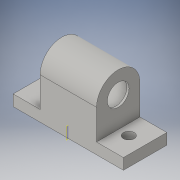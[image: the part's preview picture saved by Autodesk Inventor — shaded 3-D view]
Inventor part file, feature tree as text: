
AUTODESK INVENTOR PART (.ipt)
format: ipt  version: 2016 (Build 200138000, 138)  size: 147,968 bytes
history: native  units: in
note: dims shown in document units (in); Inventor stores cm internally (conversion verified against a paired STEP export)
features: extrude x4, sketch x4, projected_geometry x3, plane x1
ambient origin geometry x8: Origin, YZ Plane, XZ Plane, XY Plane, X Axis, Y Axis, Z Axis, Center Point
bodies: Solid1 (feature_tree)
feature tree (12):
  extrude  "Extrusion1"  Depth=0.7874in
  plane  "Work Plane1"
  extrude  "Extrusion2"  Depth=0.1969in
  extrude  "Extrusion3"  Depth=0.2953in
  extrude  "Extrusion4"  Depth=0.0394in
  sketch  "Sketch1"  dims[d0=2.0in d1=0.7874in]
  sketch  "Sketch2"  dims[d2=0.1969in d3=0.1969in]
  projected_geometry  "Projected Loop1"
  sketch  "Sketch3"  dims[d4=0.2953in d5=0.2953in]
  projected_geometry  "Projected Loop2"
  sketch  "Sketch4"  dims[d6=0.2in d7=0.0in d10=0.1in d11=0.25in d12=0.2953in d13=0.5906in d14=0.9449in d15=0.0in d16=0.3937in d17=0.0394in d18=0.0in d19=0.0394in d20=0.0in]
  projected_geometry  "Projected Loop3"
